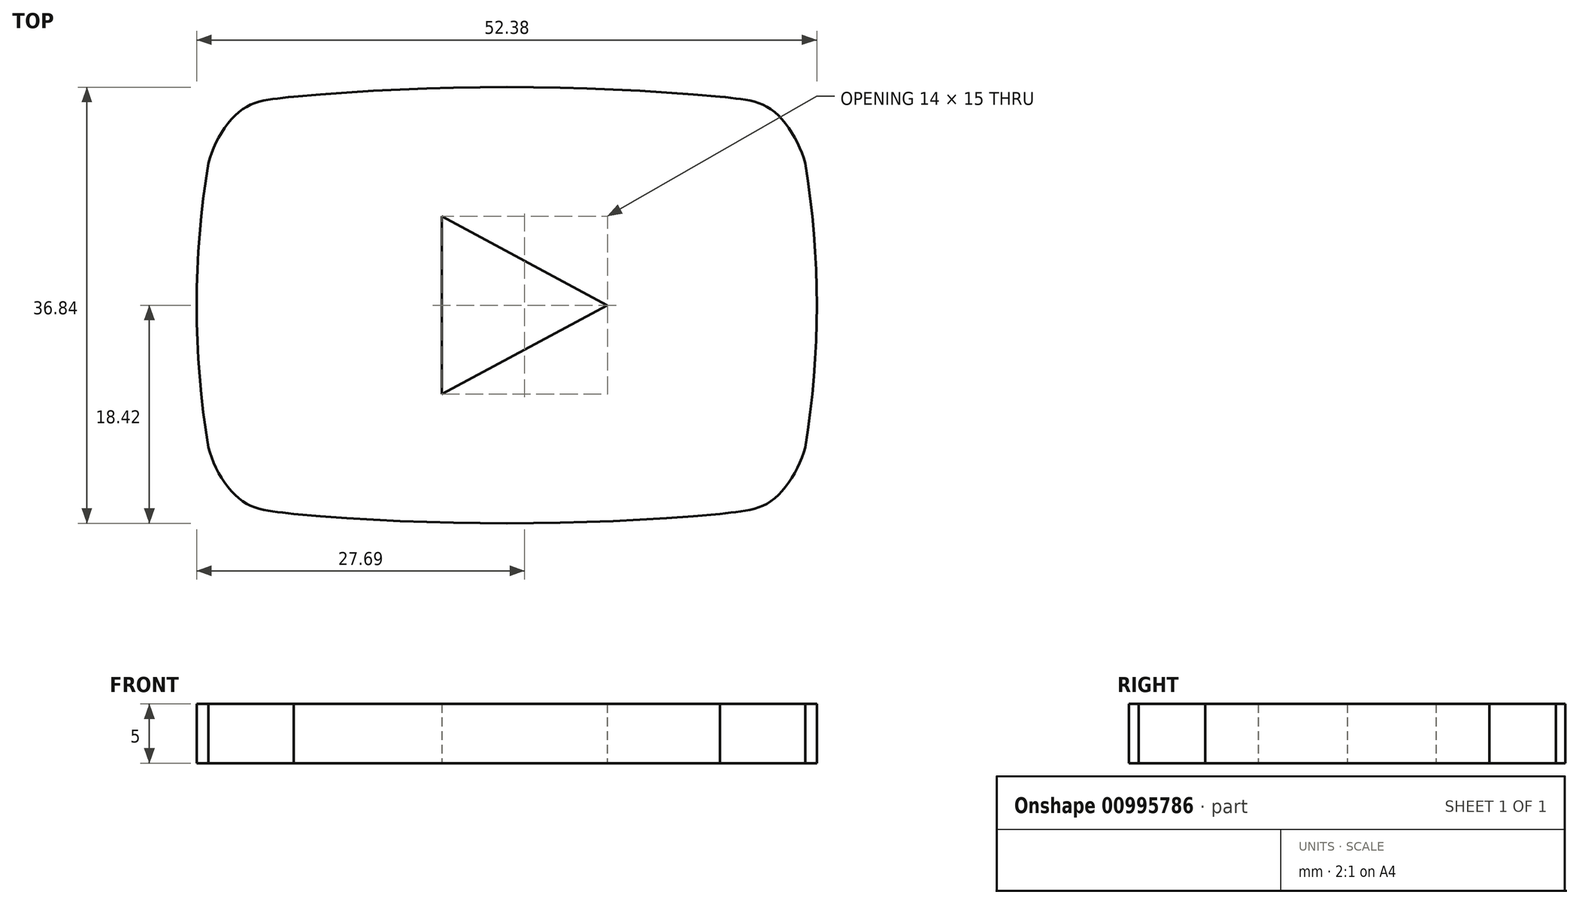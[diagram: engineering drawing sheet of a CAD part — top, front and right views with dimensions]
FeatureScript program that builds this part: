
annotation { "Feature Type Name" : "Feature", "Feature Type Description" : "" }
export const myFeature = defineFeature(function(context is Context, id is Id, definition is map)
    precondition{}
    {
        {
            var Q0;
            Q0=qCreatedBy(makeId("Top.planeOp"),FACE);
            var sketch = newSketch(context, id + "F0", { "sketchPlane" : qUnion([Q0])});
            skPoint(sketch, "E0.middle", {"position": v(0, 0) * mm});
            skLineSegment(sketch, "E1", {"start": v(0, -18.42) * mm, "end": v(0, 18.42) * mm, "construction": true});
            skLineSegment(sketch, "E2", {"start": v(-30, 0) * mm, "end": v(30, 0) * mm, "construction": true});
            skArc(sketch, "E3", {"start": v(-25.2, 12) * mm, "mid": v(-26.2, 0) * mm, "end": v(-25.2, -12) * mm});
            skArc(sketch, "E4", {"start": v(18, 17.62) * mm, "mid": v(0, 18.42) * mm, "end": v(-18, 17.62) * mm});
            skFitSpline(sketch, "E5", {"points": [v(-25.2, 12) * mm, v(-22.27, 16.57) * mm, v(-18, 17.62) * mm], "startDerivative": vector(2.45, 9.87) * mm, "endDerivative": vector(11.01, 1.4) * mm});
            skFitSpline(sketch, "E6.MirrorCS", {"points": [v(25.2, 12) * mm, v(22.27, 16.57) * mm, v(18, 17.62) * mm], "startDerivative": vector(-2.45, 9.87) * mm, "endDerivative": vector(-11.01, 1.4) * mm});
            skArc(sketch, "E7.MirrorCS", {"start": v(25.2, 12) * mm, "mid": v(26.2, 0) * mm, "end": v(25.2, -12) * mm});
            skFitSpline(sketch, "E8.MirrorCS", {"points": [v(25.2, -12) * mm, v(22.27, -16.57) * mm, v(18, -17.62) * mm], "startDerivative": vector(-2.45, -9.87) * mm, "endDerivative": vector(-11.01, -1.4) * mm});
            skArc(sketch, "E9.MirrorCS", {"start": v(18, -17.62) * mm, "mid": v(0, -18.42) * mm, "end": v(-18, -17.62) * mm});
            skFitSpline(sketch, "E10.MirrorCS", {"points": [v(-25.2, -12) * mm, v(-22.27, -16.57) * mm, v(-18, -17.62) * mm], "startDerivative": vector(2.45, -9.87) * mm, "endDerivative": vector(11.01, -1.4) * mm});
            skLineSegment(sketch, "E11", {"start": v(-5.5, 7.5) * mm, "end": v(-5.5, -7.5) * mm});
            skLineSegment(sketch, "E12", {"start": v(-5.5, -7.5) * mm, "end": v(8.5, 0) * mm});
            skLineSegment(sketch, "E13", {"start": v(8.5, 0) * mm, "end": v(-5.5, 7.5) * mm});
            skSolve(sketch);
        }
        {
            var Q0;
            Q0 = qSketchRegion(id + "F0", true);
            extrude(context, id + "F1", {"entities" : qUnion([Q0]), "depth" : 5 * mm, "offsetDistance" : 25 * mm});
        }
    });
